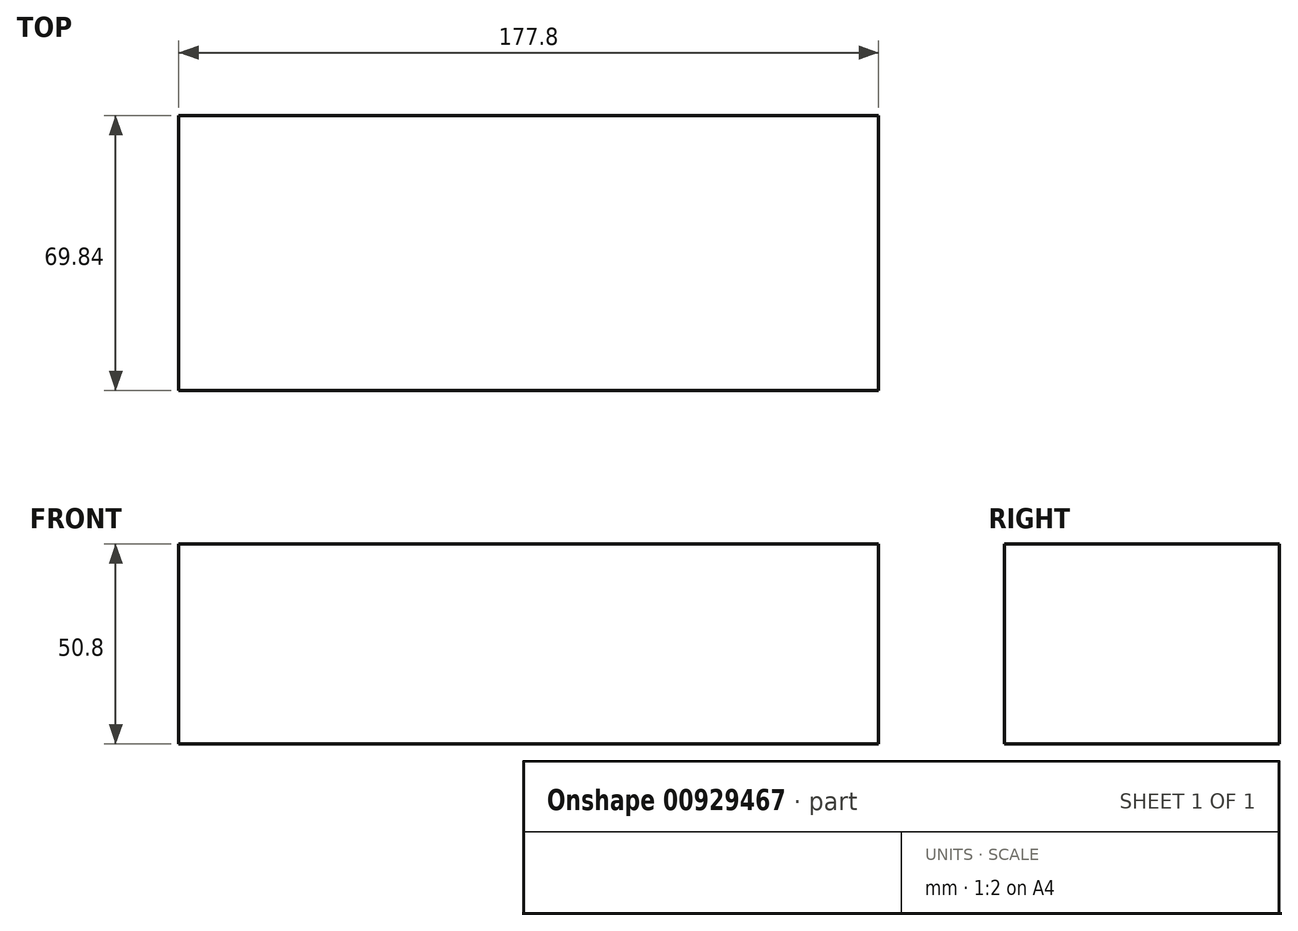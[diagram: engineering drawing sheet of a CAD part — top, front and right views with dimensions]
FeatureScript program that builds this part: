
annotation { "Feature Type Name" : "Feature", "Feature Type Description" : "" }
export const myFeature = defineFeature(function(context is Context, id is Id, definition is map)
    precondition{}
    {
        {
            var Q0;
            Q0=qCreatedBy(makeId("Top.planeOp"),FACE);
            var sketch = newSketch(context, id + "F0", { "sketchPlane" : qUnion([Q0])});
            skLineSegment(sketch, "E0.bottom", {"start": v(-88.9, -34.93) * mm, "end": v(88.9, -34.93) * mm});
            skLineSegment(sketch, "E0.top", {"start": v(-88.9, 34.93) * mm, "end": v(88.9, 34.93) * mm});
            skLineSegment(sketch, "E0.left", {"start": v(-88.9, -34.93) * mm, "end": v(-88.9, 34.93) * mm});
            skLineSegment(sketch, "E0.right", {"start": v(88.9, -34.93) * mm, "end": v(88.9, 34.93) * mm});
            skPoint(sketch, "E0.middle", {"position": v(0, 0) * mm});
            skSolve(sketch);
        }
        {
            var Q0;
            Q0=makeQuery(id+"F0.imprint","IMPRINT",FACE,{"disambiguationData":[TD([[makeQuery(id+"F0.imprint","IMPRINT",EDGE,{"derivedFrom":sQuery(id+"F0.wireOp",EDGE,"E0.bottom")}),1.0]])]});
            extrude(context, id + "F1", {"entities" : qUnion([Q0]), "depth" : 50.8 * mm, "offsetDistance" : 25.4 * mm});
        }
    });
